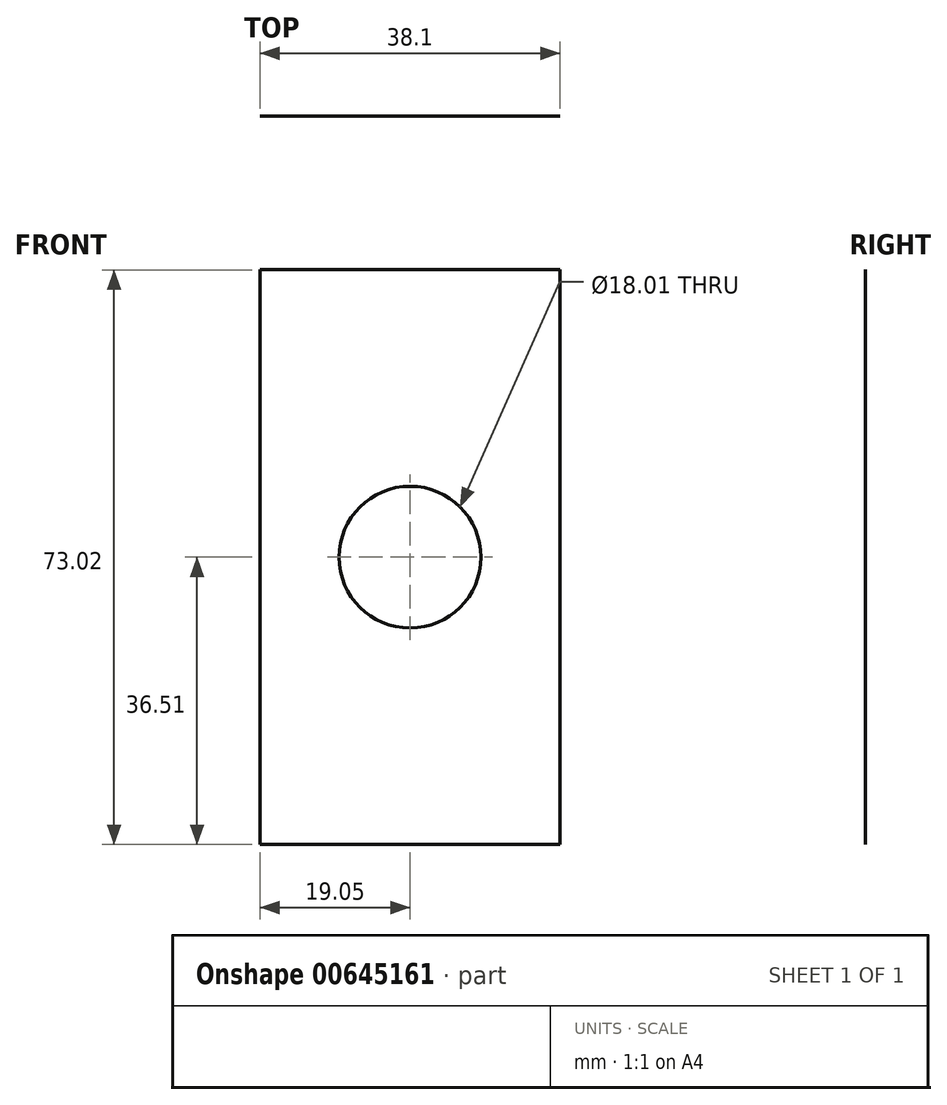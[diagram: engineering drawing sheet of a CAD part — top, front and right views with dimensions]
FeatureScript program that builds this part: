
annotation { "Feature Type Name" : "Feature", "Feature Type Description" : "" }
export const myFeature = defineFeature(function(context is Context, id is Id, definition is map)
    precondition{}
    {
        {
            var Q0;
            Q0=qCreatedBy(makeId("Front.planeOp"),FACE);
            var sketch = newSketch(context, id + "F0", { "sketchPlane" : qUnion([Q0])});
            skLineSegment(sketch, "E0.bottom", {"start": v(19.05, 36.51) * mm, "end": v(-19.05, 36.51) * mm});
            skLineSegment(sketch, "E0.top", {"start": v(19.05, -36.51) * mm, "end": v(-19.05, -36.51) * mm});
            skLineSegment(sketch, "E0.left", {"start": v(19.05, 36.51) * mm, "end": v(19.05, -36.51) * mm});
            skLineSegment(sketch, "E0.right", {"start": v(-19.05, 36.51) * mm, "end": v(-19.05, -36.51) * mm});
            skPoint(sketch, "E0.middle", {"position": v(0, 0) * mm});
            skSolve(sketch);
        }
        {
            var Q0;
            Q0=makeQuery(id+"F0.imprint","IMPRINT",FACE,{"disambiguationData":[TD([[makeQuery(id+"F0.imprint","IMPRINT",EDGE,{"derivedFrom":sQuery(id+"F0.wireOp",EDGE,"E0.bottom")}),1.0]])]});
            extrude(context, id + "F1", {"entities" : qUnion([Q0]), "depth" : 1 / 406.4 * mm, "offsetDistance" : 25.4 * mm});
        }
        {
            var Q0;
            Q0=makeQuery(id+"F1.opExtrude","CAP_FACE",FACE,{"disambiguationData":[OSD([sQuery(id+"F0.wireOp",EDGE,"E0.bottom"),sQuery(id+"F0.wireOp",EDGE,"E0.top"),sQuery(id+"F0.wireOp",EDGE,"E0.left"),sQuery(id+"F0.wireOp",EDGE,"E0.right")])],"isStart":false});
            var sketch = newSketch(context, id + "F2", { "sketchPlane" : qUnion([Q0])});
            skCircle(sketch, "E1", {"center": v(0, 0) * mm, "radius": 9 * mm});
            skSolve(sketch);
        }
        {
            var Q0;
            Q0=makeQuery(id+"F2.imprint","IMPRINT",FACE,{"disambiguationData":[TD([[makeQuery(id+"F2.imprint","IMPRINT",EDGE,{"derivedFrom":sQuery(id+"F2.wireOp",EDGE,"E1")}),1.0]])]});
            extrude(context, id + "F3", {"entities" : qUnion([Q0]), "operationType" : NewBodyOperationType.REMOVE, "oppositeDirection" : true, "depth" : 25.4 * mm, "offsetDistance" : 25.4 * mm});
        }
    });
